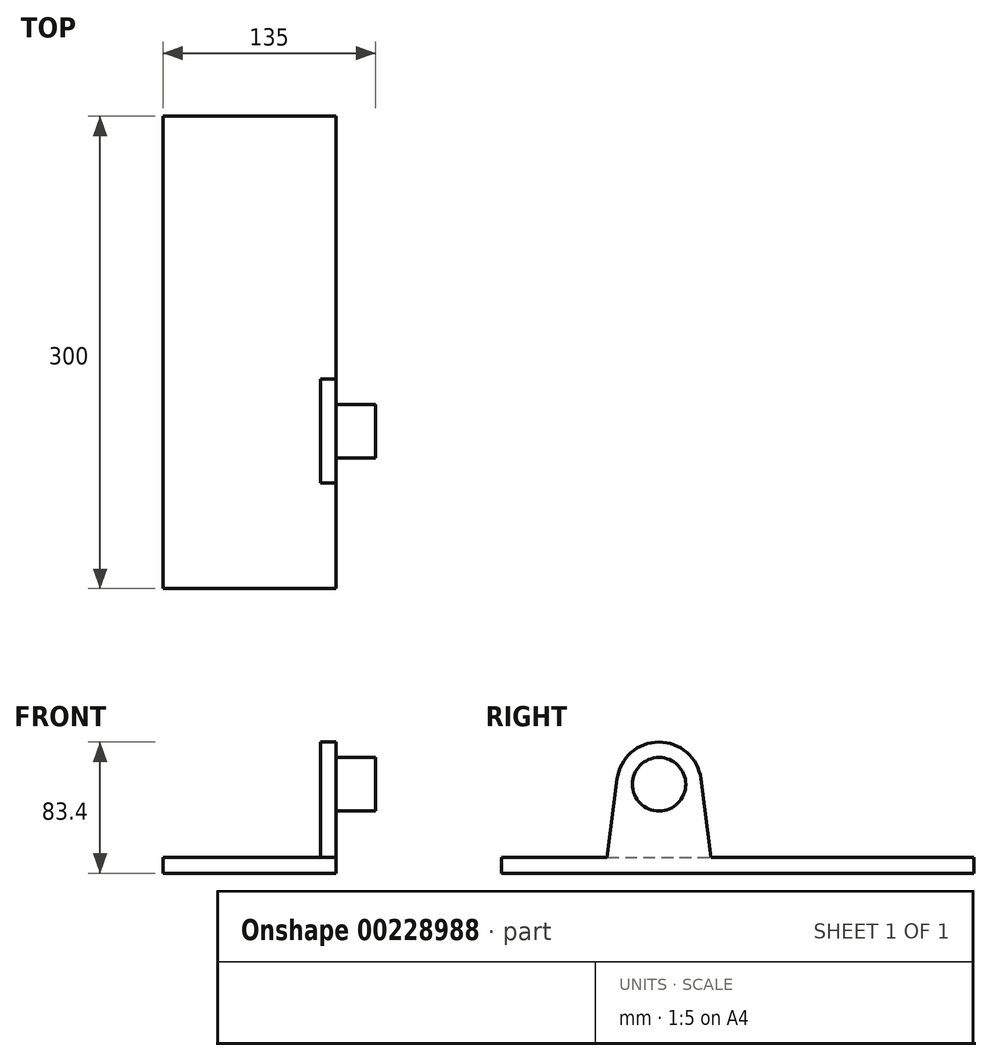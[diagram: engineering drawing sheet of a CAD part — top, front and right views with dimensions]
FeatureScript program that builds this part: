
annotation { "Feature Type Name" : "Feature", "Feature Type Description" : "" }
export const myFeature = defineFeature(function(context is Context, id is Id, definition is map)
    precondition{}
    {
        {
            var Q0;
            Q0=qCreatedBy(makeId("Top.planeOp"),FACE);
            var sketch = newSketch(context, id + "F4", { "sketchPlane" : qUnion([Q0])});
            skLineSegment(sketch, "E0.bottom", {"start": v(210, -100) * mm, "end": v(100, -100) * mm});
            skLineSegment(sketch, "E0.top", {"start": v(210, 200) * mm, "end": v(100, 200) * mm});
            skLineSegment(sketch, "E0.left", {"start": v(210, -100) * mm, "end": v(210, 200) * mm});
            skLineSegment(sketch, "E0.right", {"start": v(100, -100) * mm, "end": v(100, 200) * mm});
            skLineSegment(sketch, "E1", {"start": v(0, 365.45) * mm, "end": v(0, -365.45) * mm, "construction": true});
            skLineSegment(sketch, "E2", {"start": v(-275.83, 0) * mm, "end": v(275.83, 0) * mm, "construction": true});
            skSolve(sketch);
        }
        {
            var Q0;
            Q0=qSketchRegion(id+"F4",true);
            extrude(context, id + "F5", {"entities" : qUnion([Q0]), "oppositeDirection" : true, "depth" : 10 * mm});
        }
        {
            var Q0;
            Q0=makeQuery(id+"F5.opExtrude","SWEPT_FACE",FACE,{"disambiguationData":[OSD([sQuery(id+"F4.wireOp",EDGE,"E0.left")])]});
            var sketch = newSketch(context, id + "F0", { "sketchPlane" : qUnion([Q0])});
            skLineSegment(sketch, "E3", {"start": v(0, -10) * mm, "end": v(0, 46.58) * mm, "construction": true});
            skCircle(sketch, "E4", {"center": v(0, 46.58) * mm, "radius": 16.99 * mm});
            skArc(sketch, "E5", {"start": v(-26.6, 49.96) * mm, "mid": v(0, 73.4) * mm, "end": v(26.6, 49.96) * mm});
            skLineSegment(sketch, "E6", {"start": v(-26.6, 49.96) * mm, "end": v(-34.21, -10) * mm});
            skLineSegment(sketch, "E7", {"start": v(34.21, -10) * mm, "end": v(26.6, 49.96) * mm});
            skSolve(sketch);
        }
        {
            var Q0;
            Q0=qSketchRegion(id+"F0",true);
            var Q1;
            Q1=makeQuery(id+"F0.imprint","IMPRINT",FACE,{"disambiguationData":[TD([[makeQuery(id+"F0.imprint","IMPRINT",EDGE,{"derivedFrom":sQuery(id+"F0.wireOp",EDGE,"E4")}),-1.0]])]});
            extrude(context, id + "F1", {"entities" : qUnion([Q0, Q1]), "operationType" : NewBodyOperationType.ADD, "oppositeDirection" : true, "depth" : 10 * mm});
        }
        {
            var Q0;
            Q0=qSketchRegion(id+"F0",true);
            extrude(context, id + "F2", {"entities" : qUnion([Q0]), "operationType" : NewBodyOperationType.ADD, "depth" : 25 * mm});
        }
    });
